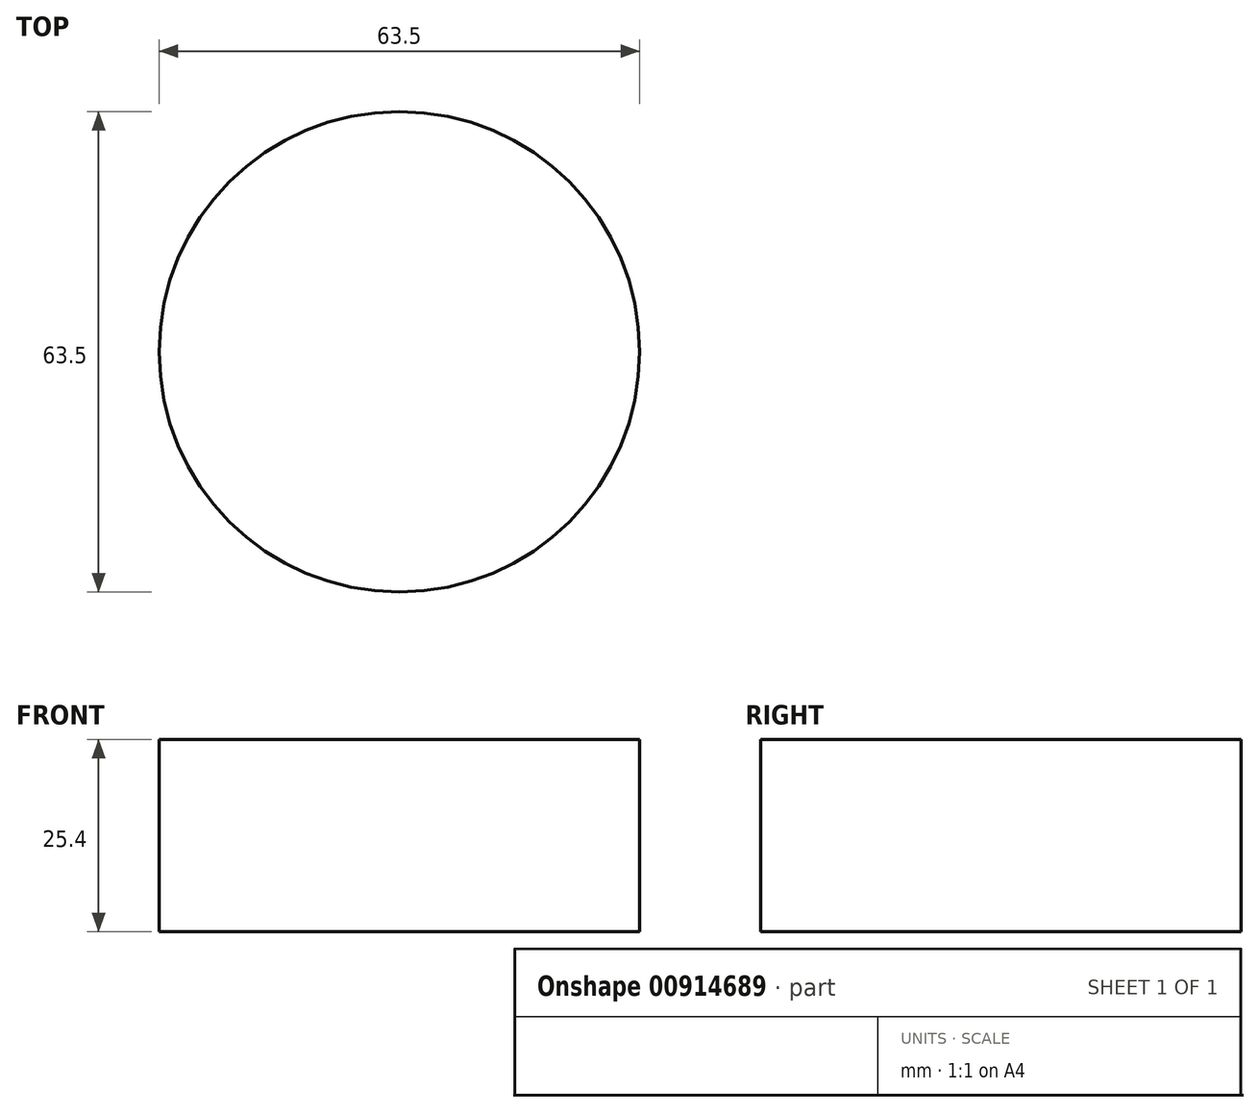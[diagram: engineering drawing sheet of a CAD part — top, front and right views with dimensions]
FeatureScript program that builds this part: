
annotation { "Feature Type Name" : "Feature", "Feature Type Description" : "" }
export const myFeature = defineFeature(function(context is Context, id is Id, definition is map)
    precondition{}
    {
        {
            var Q0;
            Q0=qCreatedBy(makeId("Top.planeOp"),FACE);
            var sketch = newSketch(context, id + "F0", { "sketchPlane" : qUnion([Q0])});
            skCircle(sketch, "E0", {"center": v(0, 0) * mm, "radius": 31.75 * mm});
            skSolve(sketch);
        }
        {
            var Q0;
            Q0 = qSketchRegion(id + "F0", true);
            var Q1;
            Q1=makeQuery(id+"F0.imprint","IMPRINT",FACE,{"disambiguationData":[TD([[makeQuery(id+"F0.imprint","IMPRINT",EDGE,{"derivedFrom":sQuery(id+"F0.wireOp",EDGE,"E0")}),1.0]])]});
            extrude(context, id + "F1", {"entities" : qUnion([Q0, Q1]), "depth" : 25.4 * mm, "offsetDistance" : 25.4 * mm});
        }
    });
